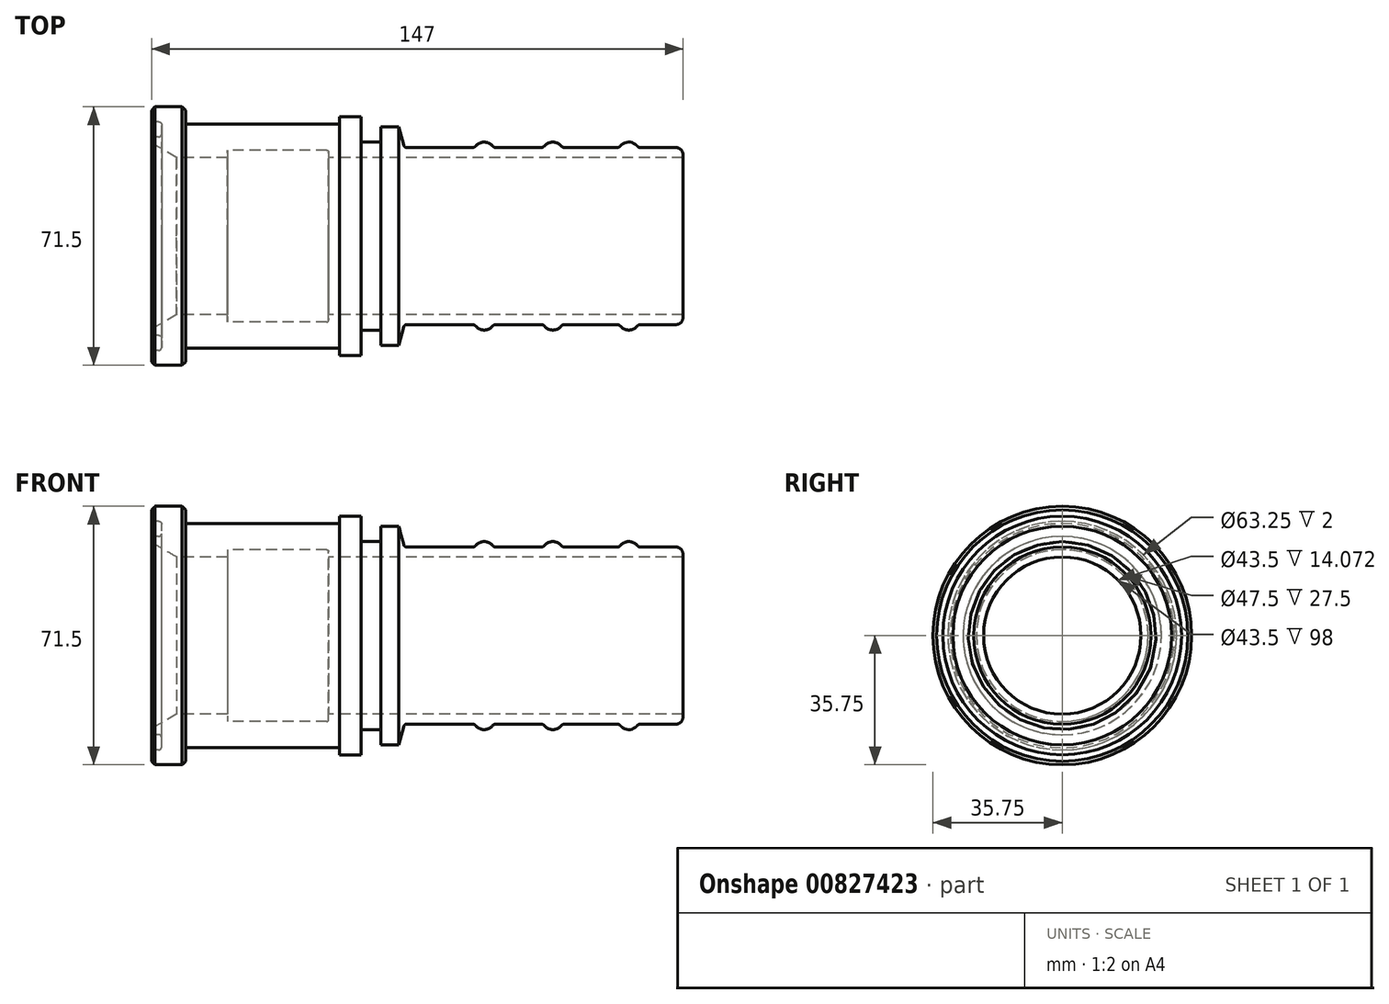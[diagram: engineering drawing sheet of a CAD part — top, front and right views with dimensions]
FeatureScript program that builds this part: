
annotation { "Feature Type Name" : "Feature", "Feature Type Description" : "" }
export const myFeature = defineFeature(function(context is Context, id is Id, definition is map)
    precondition{}
    {
        {
            var Q0;
            Q0=qCreatedBy(makeId("Front.planeOp"),FACE);
            var sketch = newSketch(context, id + "F0", { "sketchPlane" : qUnion([Q0])});
            skLineSegment(sketch, "E0", {"start": v(0, 0) * mm, "end": v(88.97, 0) * mm, "construction": true});
            skLineSegment(sketch, "E1", {"start": v(147, 21.75) * mm, "end": v(49, 21.75) * mm});
            skLineSegment(sketch, "E2", {"start": v(0, 25.75) * mm, "end": v(0, 27.42) * mm});
            skLineSegment(sketch, "E3", {"start": v(0, 35.75) * mm, "end": v(9.5, 35.75) * mm});
            skLineSegment(sketch, "E4", {"start": v(9.5, 35.75) * mm, "end": v(9.5, 31) * mm});
            skLineSegment(sketch, "E5", {"start": v(9.5, 31) * mm, "end": v(52, 31) * mm});
            skLineSegment(sketch, "E6", {"start": v(52, 31) * mm, "end": v(52, 33) * mm});
            skLineSegment(sketch, "E7", {"start": v(52, 33) * mm, "end": v(58, 33) * mm});
            skLineSegment(sketch, "E8", {"start": v(58, 33) * mm, "end": v(58, 26) * mm});
            skLineSegment(sketch, "E9", {"start": v(58, 26) * mm, "end": v(63.4, 26) * mm});
            skLineSegment(sketch, "E10", {"start": v(63.4, 26) * mm, "end": v(63.4, 30.25) * mm});
            skLineSegment(sketch, "E11", {"start": v(63.4, 30.25) * mm, "end": v(68.4, 30.25) * mm});
            skLineSegment(sketch, "E12", {"start": v(68.4, 30.25) * mm, "end": v(69.94, 24.5) * mm});
            skLineSegment(sketch, "E13", {"start": v(69.94, 24.5) * mm, "end": v(89.4, 24.5) * mm});
            skLineSegment(sketch, "E14", {"start": v(0, 25.75) * mm, "end": v(6.93, 21.75) * mm});
            skPoint(sketch, "E15.orphan", {"position": v(0, 21.75) * mm});
            skLineSegment(sketch, "E16", {"start": v(21, 21.75) * mm, "end": v(21, 23.75) * mm});
            skLineSegment(sketch, "E17", {"start": v(21, 23.75) * mm, "end": v(49, 23.75) * mm});
            skLineSegment(sketch, "E18", {"start": v(49, 23.75) * mm, "end": v(49, 21.75) * mm});
            skLineSegment(sketch, "E19.trimOffspring", {"start": v(21, 21.75) * mm, "end": v(6.93, 21.75) * mm});
            skLineSegment(sketch, "E20", {"start": v(0, 31.62) * mm, "end": v(2.8, 31.62) * mm});
            skLineSegment(sketch, "E21", {"start": v(2.8, 31.62) * mm, "end": v(2.8, 27.42) * mm});
            skLineSegment(sketch, "E22", {"start": v(2.8, 27.42) * mm, "end": v(0, 27.42) * mm});
            skLineSegment(sketch, "E23.trimOffspring", {"start": v(0, 31.62) * mm, "end": v(0, 35.75) * mm});
            skArc(sketch, "E24", {"start": v(94.6, 24.5) * mm, "mid": v(92, 26) * mm, "end": v(89.4, 24.5) * mm});
            skArc(sketch, "E25", {"start": v(113.6, 24.5) * mm, "mid": v(111, 26) * mm, "end": v(108.4, 24.5) * mm});
            skArc(sketch, "E26", {"start": v(134.6, 24.5) * mm, "mid": v(132, 26) * mm, "end": v(129.4, 24.5) * mm});
            skLineSegment(sketch, "E27", {"start": v(147, 21.75) * mm, "end": v(147, 24.5) * mm});
            skLineSegment(sketch, "E28.trimOffspring", {"start": v(94.6, 24.5) * mm, "end": v(108.4, 24.5) * mm});
            skLineSegment(sketch, "E29.trimOffspring", {"start": v(113.6, 24.5) * mm, "end": v(129.4, 24.5) * mm});
            skLineSegment(sketch, "E30.trimOffspring", {"start": v(134.6, 24.5) * mm, "end": v(147, 24.5) * mm});
            skSolve(sketch);
        }
        {
            var Q0;
            Q0=makeQuery(id+"F0.imprint","IMPRINT",FACE,{"disambiguationData":[TD([[makeQuery(id+"F0.imprint","IMPRINT",EDGE,{"derivedFrom":sQuery(id+"F0.wireOp",EDGE,"E1")}),-1.0]])]});
            var Q1;
            Q1=sQuery(id+"F0.wireOp",EDGE,"E0");
            revolve(context, id + "F1", {"surfaceOperationType" : NewSurfaceOperationType.NEW, "entities" : qUnion([Q0]), "axis" : qUnion([Q1]), "revolveType" : RevolveType.FULL});
        }
        {
            var Q0;
            Q0=makeQuery(id+"F1.opRevolve","SWEPT_EDGE",EDGE,{"disambiguationData":[OSD([sQuery(id+"F0.wireOp",EDGE,"E26"),sQuery(id+"F0.wireOp",EDGE,"E30.trimOffspring")])]});
            var Q1;
            Q1=makeQuery(id+"F1.opRevolve","SWEPT_EDGE",EDGE,{"disambiguationData":[OSD([sQuery(id+"F0.wireOp",EDGE,"E25"),sQuery(id+"F0.wireOp",EDGE,"E29.trimOffspring")])]});
            var Q2;
            Q2=makeQuery(id+"F1.opRevolve","SWEPT_EDGE",EDGE,{"disambiguationData":[OSD([sQuery(id+"F0.wireOp",EDGE,"E24"),sQuery(id+"F0.wireOp",EDGE,"E28.trimOffspring")])]});
            var Q3;
            Q3=makeQuery(id+"F1.opRevolve","SWEPT_EDGE",EDGE,{"disambiguationData":[OSD([sQuery(id+"F0.wireOp",EDGE,"E13"),sQuery(id+"F0.wireOp",EDGE,"E24")])]});
            var Q4;
            Q4=makeQuery(id+"F1.opRevolve","SWEPT_EDGE",EDGE,{"disambiguationData":[OSD([sQuery(id+"F0.wireOp",EDGE,"E25"),sQuery(id+"F0.wireOp",EDGE,"E28.trimOffspring")])]});
            var Q5;
            Q5=makeQuery(id+"F1.opRevolve","SWEPT_EDGE",EDGE,{"disambiguationData":[OSD([sQuery(id+"F0.wireOp",EDGE,"E26"),sQuery(id+"F0.wireOp",EDGE,"E29.trimOffspring")])]});
            fillet(context, id + "F2", {"entities" : qUnion([Q0, Q1, Q2, Q3, Q4, Q5]), "radius" : 1.2 * mm, "tangentPropagation" : true, "allowEdgeOverflow" : false});
        }
        {
            var Q0;
            Q0=makeQuery(id+"F1.opRevolve","SWEPT_EDGE",EDGE,{"disambiguationData":[OSD([sQuery(id+"F0.wireOp",EDGE,"E27"),sQuery(id+"F0.wireOp",EDGE,"E30.trimOffspring")])]});
            fillet(context, id + "F3", {"entities" : qUnion([Q0]), "radius" : 2 * mm, "tangentPropagation" : true, "allowEdgeOverflow" : false});
        }
        {
            var Q0;
            Q0=makeQuery(id+"F1.opRevolve","SWEPT_EDGE",EDGE,{"disambiguationData":[OSD([sQuery(id+"F0.wireOp",EDGE,"E12"),sQuery(id+"F0.wireOp",EDGE,"E13")])]});
            fillet(context, id + "F4", {"entities" : qUnion([Q0]), "radius" : .8 * mm, "tangentPropagation" : true, "allowEdgeOverflow" : false});
        }
        {
            var Q0;
            Q0=makeQuery(id+"F1.opRevolve","SWEPT_EDGE",EDGE,{"disambiguationData":[OSD([sQuery(id+"F0.wireOp",EDGE,"E8"),sQuery(id+"F0.wireOp",EDGE,"E9")])]});
            var Q1;
            Q1=makeQuery(id+"F1.opRevolve","SWEPT_EDGE",EDGE,{"disambiguationData":[OSD([sQuery(id+"F0.wireOp",EDGE,"E9"),sQuery(id+"F0.wireOp",EDGE,"E10")])]});
            fillet(context, id + "F5", {"entities" : qUnion([Q0, Q1]), "radius" : .4 * mm, "tangentPropagation" : true, "allowEdgeOverflow" : false});
        }
        {
            var Q0;
            Q0=makeQuery(id+"F1.opRevolve","SWEPT_EDGE",EDGE,{"disambiguationData":[OSD([sQuery(id+"F0.wireOp",EDGE,"E17"),sQuery(id+"F0.wireOp",EDGE,"E18")])]});
            fillet(context, id + "F6", {"entities" : qUnion([Q0]), "radius" : .5 * mm, "tangentPropagation" : true, "allowEdgeOverflow" : false});
        }
        {
            var Q0;
            Q0=makeQuery(id+"F1.opRevolve","SWEPT_EDGE",EDGE,{"disambiguationData":[OSD([sQuery(id+"F0.wireOp",EDGE,"E20"),sQuery(id+"F0.wireOp",EDGE,"E21")])]});
            var Q1;
            Q1=makeQuery(id+"F1.opRevolve","SWEPT_EDGE",EDGE,{"disambiguationData":[OSD([sQuery(id+"F0.wireOp",EDGE,"E21"),sQuery(id+"F0.wireOp",EDGE,"E22")])]});
            fillet(context, id + "F7", {"entities" : qUnion([Q0, Q1]), "radius" : .8 * mm, "tangentPropagation" : true, "allowEdgeOverflow" : false});
        }
        {
            var Q0;
            Q0=makeQuery(id+"F1.opRevolve","SWEPT_EDGE",EDGE,{"disambiguationData":[OSD([sQuery(id+"F0.wireOp",EDGE,"E3"),sQuery(id+"F0.wireOp",EDGE,"E4")])]});
            var Q1;
            Q1=makeQuery(id+"F1.opRevolve","SWEPT_EDGE",EDGE,{"disambiguationData":[OSD([sQuery(id+"F0.wireOp",EDGE,"E3"),sQuery(id+"F0.wireOp",EDGE,"E23.trimOffspring")])]});
            chamfer(context, id + "F8", {"entities" : qUnion([Q0, Q1]), "width" : 1 * mm, "tangentPropagation" : true});
        }
    });
